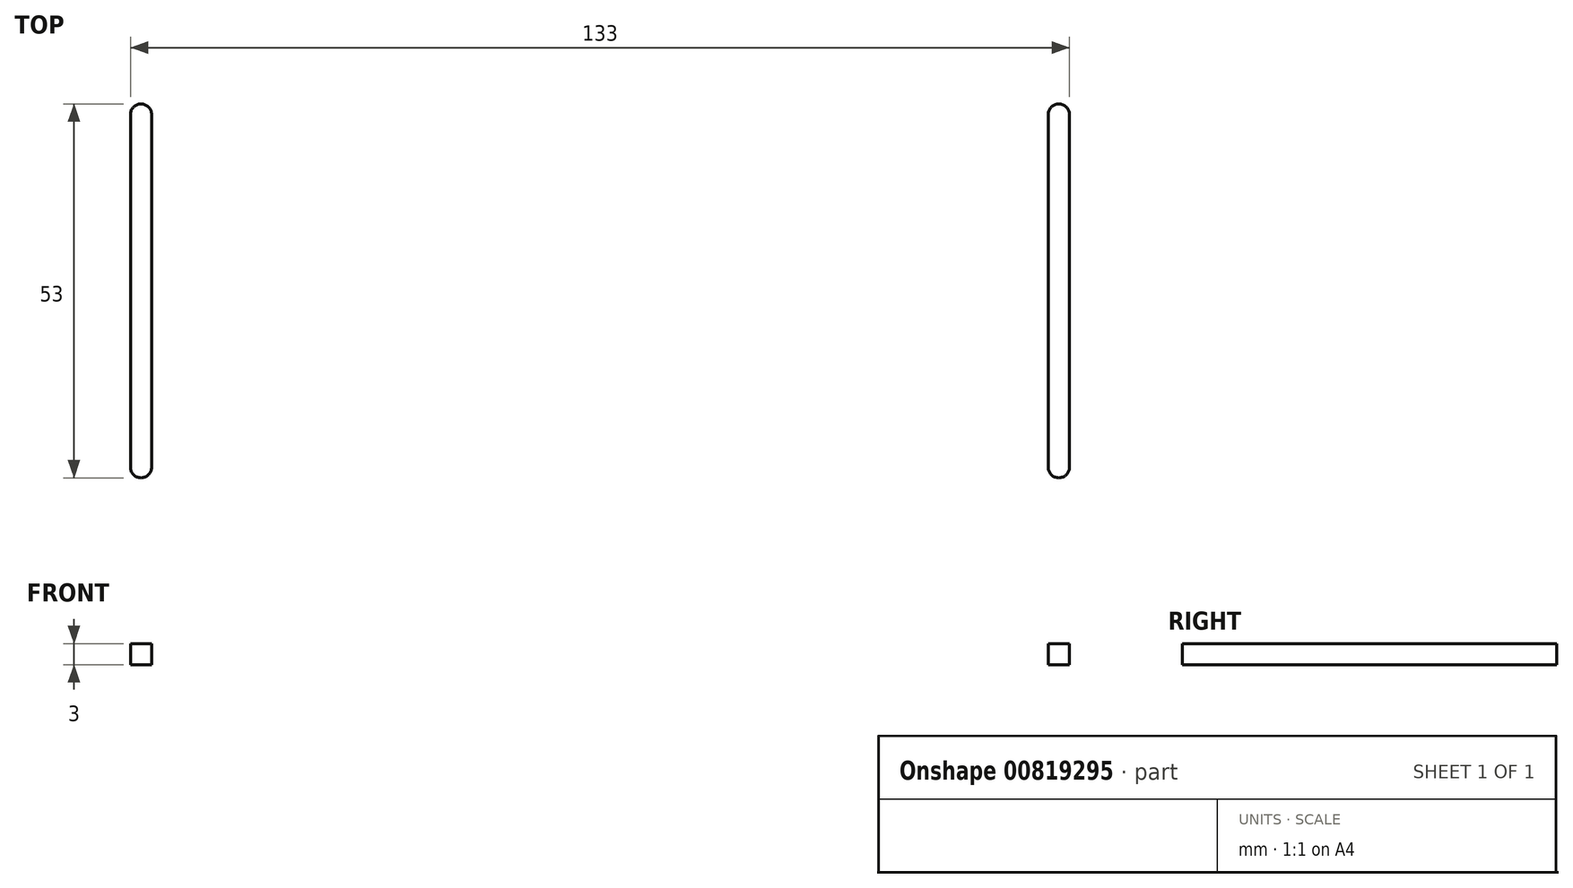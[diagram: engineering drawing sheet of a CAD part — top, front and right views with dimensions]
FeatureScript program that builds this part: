
annotation { "Feature Type Name" : "Feature", "Feature Type Description" : "" }
export const myFeature = defineFeature(function(context is Context, id is Id, definition is map)
    precondition{}
    {
        {
            var Q0;
            Q0=qCreatedBy(makeId("Top.planeOp"),FACE);
            var sketch = newSketch(context, id + "F0", { "sketchPlane" : qUnion([Q0])});
            skLineSegment(sketch, "E0.bottom", {"start": v(0, 0) * mm, "end": v(70, 0) * mm});
            skLineSegment(sketch, "E0.top", {"start": v(0, 140) * mm, "end": v(70, 140) * mm});
            skLineSegment(sketch, "E0.left", {"start": v(0, 0) * mm, "end": v(0, 140) * mm});
            skLineSegment(sketch, "E0.right", {"start": v(70, 0) * mm, "end": v(70, 140) * mm});
            skSolve(sketch);
        }
        {
            var Q0;
            Q0 = qSketchRegion(id + "F0", true);
            extrude(context, id + "F1", {"entities" : qUnion([Q0]), "depth" : 3 * mm, "offsetDistance" : 25 * mm});
        }
        {
            var Q0;
            Q0=makeQuery(id+"F1.opExtrude","CAP_FACE",FACE,{"disambiguationData":[OSD([sQuery(id+"F0.wireOp",EDGE,"E0.bottom"),sQuery(id+"F0.wireOp",EDGE,"E0.top"),sQuery(id+"F0.wireOp",EDGE,"E0.left"),sQuery(id+"F0.wireOp",EDGE,"E0.right")])],"isStart":false});
            var sketch = newSketch(context, id + "F2", { "sketchPlane" : qUnion([Q0])});
            skLineSegment(sketch, "E1", {"start": v(50, 58) * mm, "end": v(50, 82) * mm});
            skLineSegment(sketch, "E2", {"start": v(50, 82) * mm, "end": v(50, 58) * mm});
            skSolve(sketch);
        }
        {
            var Q0;
            Q0=sQuery(id+"F2.wireOp",VERTEX,"E1.start");
            var Q1;
            Q1=sQuery(id+"F2.wireOp",VERTEX,"E1.end");
            var Q2;
            Q2=makeQuery(id+"F1.opExtrude","SWEPT_BODY",BODY,{"disambiguationData":[OSD([sQuery(id+"F0.wireOp",EDGE,"E0.bottom"),sQuery(id+"F0.wireOp",EDGE,"E0.top"),sQuery(id+"F0.wireOp",EDGE,"E0.left"),sQuery(id+"F0.wireOp",EDGE,"E0.right")])]});
            hole(context, id + "F3", {"style" : HoleStyle.SIMPLE, "endStyle" : HoleEndStyle.THROUGH, "holeDiameter" : 3 * mm, "majorDiameter" : 5 * mm, "isTappedThrough" : true, "tappedDepth" : 12 * mm, "tapClearance" : 3, "locations" : qUnion([Q0, Q1]), "scope" : qUnion([Q2])});
        }
        {
            var Q0;
            Q0=makeQuery(id+"F1.opExtrude","CAP_FACE",FACE,{"disambiguationData":[OSD([sQuery(id+"F0.wireOp",EDGE,"E0.bottom"),sQuery(id+"F0.wireOp",EDGE,"E0.top"),sQuery(id+"F0.wireOp",EDGE,"E0.left"),sQuery(id+"F0.wireOp",EDGE,"E0.right")])],"isStart":false});
            var sketch = newSketch(context, id + "F4", { "sketchPlane" : qUnion([Q0])});
            skSolve(sketch);
        }
        {
            var Q0;
            Q0=makeQuery(id+"F4.imprint","IMPRINT",FACE,{"disambiguationData":[TD([[makeQuery(id+"F4.imprint","IMPRINT",EDGE,{"derivedFrom":makeQuery(id+"F1.opExtrude","CAP_EDGE",EDGE,{"disambiguationData":[OSD([sQuery(id+"F0.wireOp",EDGE,"E0.bottom")])],"isStart":false})}),1.0]])]});
            var sketch = newSketch(context, id + "F5", { "sketchPlane" : qUnion([Q0])});
            skSolve(sketch);
        }
        {
            var Q0;
            Q0=makeQuery(id+"F4.imprint","IMPRINT",FACE,{"disambiguationData":[TD([[makeQuery(id+"F4.imprint","IMPRINT",EDGE,{"derivedFrom":makeQuery(id+"F1.opExtrude","CAP_EDGE",EDGE,{"disambiguationData":[OSD([sQuery(id+"F0.wireOp",EDGE,"E0.bottom")])],"isStart":false})}),1.0]])]});
            var sketch = newSketch(context, id + "F6", { "sketchPlane" : qUnion([Q0])});
            skLineSegment(sketch, "E3", {"start": v(65, 45) * mm, "end": v(65, 95) * mm});
            skSolve(sketch);
        }
        {
            var Q0;
            Q0=makeQuery(id+"F4.imprint","IMPRINT",FACE,{"disambiguationData":[TD([[makeQuery(id+"F4.imprint","IMPRINT",EDGE,{"derivedFrom":makeQuery(id+"F1.opExtrude","CAP_EDGE",EDGE,{"disambiguationData":[OSD([sQuery(id+"F0.wireOp",EDGE,"E0.bottom")])],"isStart":false})}),1.0]])]});
            var sketch = newSketch(context, id + "F7", { "sketchPlane" : qUnion([Q0])});
            skLineSegment(sketch, "E4.JYB.JYB", {"start": v(65, 45) * mm, "end": v(65, 95) * mm, "construction": true});
            skArc(sketch, "E4.0.startCap", {"start": v(66.5, 45) * mm, "mid": v(65, 43.5) * mm, "end": v(63.5, 45) * mm});
            skArc(sketch, "E4.0.endCap", {"start": v(63.5, 95) * mm, "mid": v(65, 96.5) * mm, "end": v(66.5, 95) * mm});
            skLineSegment(sketch, "E4.0.left", {"start": v(63.5, 45) * mm, "end": v(63.5, 95) * mm});
            skLineSegment(sketch, "E4.0.right", {"start": v(66.5, 45) * mm, "end": v(66.5, 95) * mm});
            skSolve(sketch);
        }
        {
            var Q0;
            Q0=makeQuery(id+"F4.imprint","IMPRINT",FACE,{"disambiguationData":[TD([[makeQuery(id+"F4.imprint","IMPRINT",EDGE,{"derivedFrom":makeQuery(id+"F1.opExtrude","CAP_EDGE",EDGE,{"disambiguationData":[OSD([sQuery(id+"F0.wireOp",EDGE,"E0.bottom")])],"isStart":false})}),1.0]])]});
            var sketch = newSketch(context, id + "F8", { "sketchPlane" : qUnion([Q0])});
            skLineSegment(sketch, "E5", {"start": v(17.4, 87.4) * mm, "end": v(39.27, 122.7) * mm});
            skSolve(sketch);
        }
        {
            var Q0;
            Q0=sQuery(id+"F8.wireOp",VERTEX,"E5.end");
            var Q1;
            Q1=makeQuery(id+"F1.opExtrude","SWEPT_BODY",BODY,{"disambiguationData":[OSD([sQuery(id+"F0.wireOp",EDGE,"E0.bottom"),sQuery(id+"F0.wireOp",EDGE,"E0.top"),sQuery(id+"F0.wireOp",EDGE,"E0.left"),sQuery(id+"F0.wireOp",EDGE,"E0.right")])]});
            hole(context, id + "F9", {"style" : HoleStyle.SIMPLE, "endStyle" : HoleEndStyle.THROUGH, "holeDiameter" : 3 * mm, "majorDiameter" : 5 * mm, "isTappedThrough" : true, "tappedDepth" : 12 * mm, "tapClearance" : 3, "locations" : qUnion([Q0]), "scope" : qUnion([Q1])});
        }
        {
            var Q0;
            Q0=makeQuery(id+"F5.imprint","IMPRINT",FACE,{"disambiguationData":[TD([[makeQuery(id+"F5.imprint","IMPRINT",EDGE,{"derivedFrom":makeQuery(id+"F4.imprint","IMPRINT",EDGE,{"derivedFrom":makeQuery(id+"F1.opExtrude","CAP_EDGE",EDGE,{"disambiguationData":[OSD([sQuery(id+"F0.wireOp",EDGE,"E0.bottom")])],"isStart":false})})}),1.0]])]});
            var sketch = newSketch(context, id + "F10", { "sketchPlane" : qUnion([Q0])});
            skLineSegment(sketch, "E6", {"start": v(17.96, 50.8) * mm, "end": v(9.62, 14.96) * mm});
            skSolve(sketch);
        }
        {
            var Q0;
            Q0=sQuery(id+"F10.wireOp",VERTEX,"E6.end");
            var Q1;
            Q1=makeQuery(id+"F1.opExtrude","SWEPT_BODY",BODY,{"disambiguationData":[OSD([sQuery(id+"F0.wireOp",EDGE,"E0.bottom"),sQuery(id+"F0.wireOp",EDGE,"E0.top"),sQuery(id+"F0.wireOp",EDGE,"E0.left"),sQuery(id+"F0.wireOp",EDGE,"E0.right")])]});
            hole(context, id + "F11", {"style" : HoleStyle.SIMPLE, "endStyle" : HoleEndStyle.THROUGH, "holeDiameter" : 3 * mm, "majorDiameter" : 5 * mm, "isTappedThrough" : true, "tappedDepth" : 12 * mm, "tapClearance" : 3, "locations" : qUnion([Q0]), "scope" : qUnion([Q1])});
        }
        {
            var Q0;
            Q0=makeQuery(id+"F4.imprint","IMPRINT",FACE,{"disambiguationData":[TD([[makeQuery(id+"F4.imprint","IMPRINT",EDGE,{"derivedFrom":makeQuery(id+"F1.opExtrude","CAP_EDGE",EDGE,{"disambiguationData":[OSD([sQuery(id+"F0.wireOp",EDGE,"E0.bottom")])],"isStart":false})}),1.0]])]});
            var sketch = newSketch(context, id + "F12", { "sketchPlane" : qUnion([Q0])});
            skLineSegment(sketch, "E7.bottom", {"start": v(70.13, 140.28) * mm, "end": v(56.5, 140.28) * mm});
            skLineSegment(sketch, "E7.top", {"start": v(70.13, 127.84) * mm, "end": v(56.5, 127.84) * mm});
            skLineSegment(sketch, "E7.left", {"start": v(70.13, 140.28) * mm, "end": v(70.13, 127.84) * mm});
            skLineSegment(sketch, "E7.right", {"start": v(56.5, 140.28) * mm, "end": v(56.5, 127.84) * mm});
            skSolve(sketch);
        }
        {
            var Q0;
            {var subQ0=sQuery(id+"F12.wireOp",EDGE,"E7.right");var subQ1=sQuery(id+"F12.wireOp",EDGE,"E7.top");var subQ2=makeQuery(id+"F12.imprint","INTERSECT",VERTEX,{"derivedFrom":[subQ1,subQ0]});Q0=makeQuery(id+"F12.imprint","IMPRINT",FACE,{"disambiguationData":[TD([[makeQuery(id+"F12.imprint","IMPRINT",EDGE,{"disambiguationData":[TD([[subQ2,1.0]])],"derivedFrom":subQ1}),-1.0]])]});}
            extrude(context, id + "F13", {"entities" : qUnion([Q0]), "operationType" : NewBodyOperationType.REMOVE, "oppositeDirection" : true, "depth" : 3 * mm, "offsetDistance" : 25 * mm});
        }
        {
            var Q0;
            Q0=makeQuery(id+"F6.imprint","IMPRINT",FACE,{"disambiguationData":[TD([[makeQuery(id+"F6.imprint","IMPRINT",EDGE,{"derivedFrom":makeQuery(id+"F4.imprint","IMPRINT",EDGE,{"derivedFrom":makeQuery(id+"F1.opExtrude","CAP_EDGE",EDGE,{"disambiguationData":[OSD([sQuery(id+"F0.wireOp",EDGE,"E0.bottom")])],"isStart":false})})}),1.0]])]});
            var sketch = newSketch(context, id + "F14", { "sketchPlane" : qUnion([Q0])});
            skLineSegment(sketch, "E8.bottom", {"start": v(71.4, 0) * mm, "end": v(56.4, 0) * mm});
            skLineSegment(sketch, "E8.top", {"start": v(71.4, 13.64) * mm, "end": v(56.4, 13.64) * mm});
            skLineSegment(sketch, "E8.left", {"start": v(71.4, 0) * mm, "end": v(71.4, 13.64) * mm});
            skLineSegment(sketch, "E8.right", {"start": v(56.4, 0) * mm, "end": v(56.4, 13.64) * mm});
            skSolve(sketch);
        }
        {
            var Q0;
            {var subQ3=sQuery(id+"F14.wireOp",EDGE,"E8.right");Q0=makeQuery(id+"F14.imprint","IMPRINT",FACE,{"disambiguationData":[TD([[makeQuery(id+"F14.imprint","IMPRINT",EDGE,{"derivedFrom":subQ3}),-1.0]])]});}
            extrude(context, id + "F15", {"entities" : qUnion([Q0]), "operationType" : NewBodyOperationType.REMOVE, "oppositeDirection" : true, "depth" : 4.8 * mm, "offsetDistance" : 25 * mm});
        }
        {
            var Q0;
            Q0=makeQuery(id+"F7.imprint","IMPRINT",FACE,{"disambiguationData":[TD([[makeQuery(id+"F7.imprint","IMPRINT",EDGE,{"derivedFrom":sQuery(id+"F7.wireOp",EDGE,"E4.0.startCap")}),-1.0]])]});
            extrude(context, id + "F16", {"entities" : qUnion([Q0]), "operationType" : NewBodyOperationType.REMOVE, "oppositeDirection" : true, "depth" : 36.92 * mm, "offsetDistance" : 25 * mm});
        }
        {
            var Q0;
            Q0=makeQuery(id+"F1.opExtrude","SWEPT_BODY",BODY,{"disambiguationData":[OSD([sQuery(id+"F0.wireOp",EDGE,"E0.bottom"),sQuery(id+"F0.wireOp",EDGE,"E0.top"),sQuery(id+"F0.wireOp",EDGE,"E0.left"),sQuery(id+"F0.wireOp",EDGE,"E0.right")])]});
            var Q1;
            Q1=qCreatedBy(makeId("Right.planeOp"),FACE);
            mirror(context, id + "F17", {"operationType" : NewBodyOperationType.ADD, "entities" : qUnion([Q0]), "mirrorPlane" : qUnion([Q1])});
        }
    });
